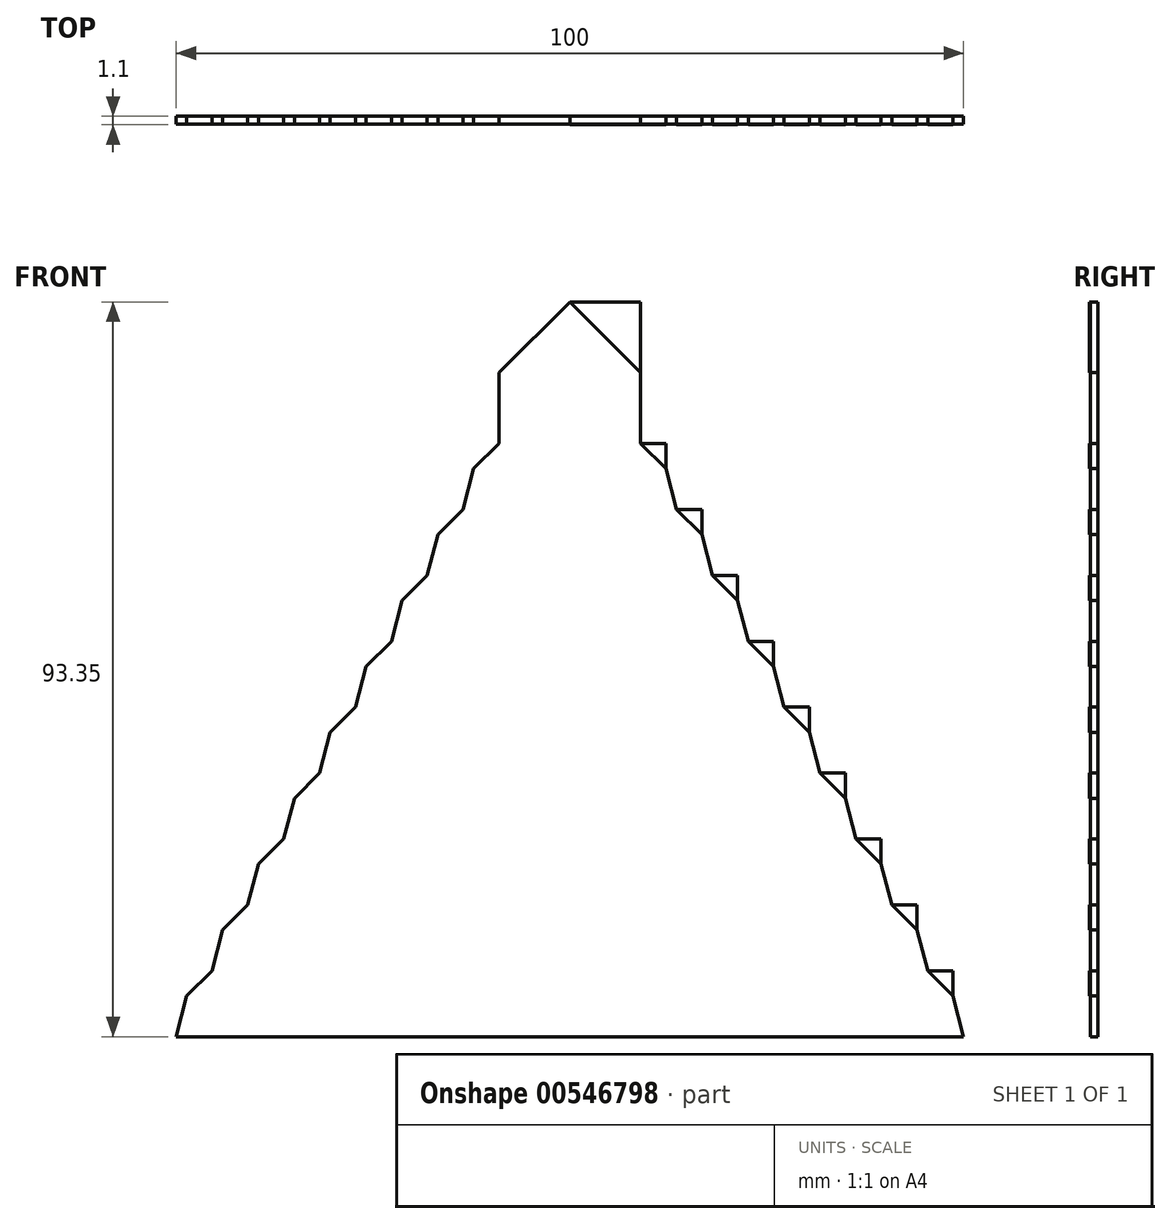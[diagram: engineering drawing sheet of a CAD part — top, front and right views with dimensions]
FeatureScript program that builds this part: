
annotation { "Feature Type Name" : "Feature", "Feature Type Description" : "" }
export const myFeature = defineFeature(function(context is Context, id is Id, definition is map)
    precondition{}
    {
        {
            var Q0;
            Q0=qCreatedBy(makeId("Front.planeOp"),FACE);
            var sketch = newSketch(context, id + "F0", { "sketchPlane" : qUnion([Q0])});
            skLineSegment(sketch, "E0.right", {"start": v(50, 0) * mm, "end": v(48.66, 5.18) * mm});
            skLineSegment(sketch, "E1", {"start": v(48.66, 5.18) * mm, "end": v(45.46, 8.38) * mm});
            skLineSegment(sketch, "E2.right", {"start": v(45.46, 8.38) * mm, "end": v(44.1, 13.55) * mm});
            skLineSegment(sketch, "E3", {"start": v(44.1, 13.55) * mm, "end": v(40.9, 16.75) * mm});
            skLineSegment(sketch, "E4.right", {"start": v(40.9, 16.75) * mm, "end": v(39.55, 21.92) * mm});
            skLineSegment(sketch, "E5", {"start": v(39.55, 21.92) * mm, "end": v(36.35, 25.12) * mm});
            skLineSegment(sketch, "E6.right", {"start": v(36.35, 25.12) * mm, "end": v(34.99, 30.3) * mm});
            skLineSegment(sketch, "E7", {"start": v(34.99, 30.3) * mm, "end": v(31.79, 33.5) * mm});
            skLineSegment(sketch, "E8.right", {"start": v(31.79, 33.5) * mm, "end": v(30.43, 38.66) * mm});
            skLineSegment(sketch, "E9", {"start": v(30.43, 38.66) * mm, "end": v(27.23, 41.86) * mm});
            skLineSegment(sketch, "E10.right", {"start": v(27.23, 41.86) * mm, "end": v(25.87, 47.04) * mm});
            skLineSegment(sketch, "E11", {"start": v(25.87, 47.04) * mm, "end": v(22.67, 50.24) * mm});
            skLineSegment(sketch, "E12.right", {"start": v(22.67, 50.24) * mm, "end": v(21.32, 55.4) * mm});
            skLineSegment(sketch, "E13", {"start": v(21.32, 55.4) * mm, "end": v(18.12, 58.6) * mm});
            skLineSegment(sketch, "E14.right", {"start": v(18.12, 58.6) * mm, "end": v(16.76, 63.78) * mm});
            skLineSegment(sketch, "E15", {"start": v(16.76, 63.78) * mm, "end": v(13.56, 66.98) * mm});
            skLineSegment(sketch, "E16.right", {"start": v(13.56, 66.98) * mm, "end": v(12.2, 72.15) * mm});
            skLineSegment(sketch, "E17", {"start": v(12.2, 72.15) * mm, "end": v(9, 75.35) * mm});
            skLineSegment(sketch, "E18", {"start": v(9, 75.35) * mm, "end": v(9, 84.35) * mm});
            skLineSegment(sketch, "E19", {"start": v(9, 84.35) * mm, "end": v(0, 93.35) * mm});
            skLineSegment(sketch, "E20", {"start": v(0, 93.35) * mm, "end": v(0, 0) * mm, "construction": true});
            skLineSegment(sketch, "E21.MirrorCS", {"start": v(-48.66, 5.18) * mm, "end": v(-45.46, 8.38) * mm});
            skLineSegment(sketch, "E22.MirrorCS", {"start": v(-45.46, 8.38) * mm, "end": v(-44.1, 13.55) * mm});
            skLineSegment(sketch, "E23.MirrorCS", {"start": v(-44.1, 13.55) * mm, "end": v(-40.9, 16.75) * mm});
            skLineSegment(sketch, "E24.MirrorCS", {"start": v(-40.9, 16.75) * mm, "end": v(-39.55, 21.92) * mm});
            skLineSegment(sketch, "E25.MirrorCS", {"start": v(-39.55, 21.92) * mm, "end": v(-36.35, 25.12) * mm});
            skLineSegment(sketch, "E26.MirrorCS", {"start": v(-36.35, 25.12) * mm, "end": v(-34.99, 30.3) * mm});
            skLineSegment(sketch, "E27.MirrorCS", {"start": v(-34.99, 30.3) * mm, "end": v(-31.79, 33.5) * mm});
            skLineSegment(sketch, "E28.MirrorCS", {"start": v(-31.79, 33.5) * mm, "end": v(-30.43, 38.66) * mm});
            skLineSegment(sketch, "E29.MirrorCS", {"start": v(-30.43, 38.66) * mm, "end": v(-27.23, 41.86) * mm});
            skLineSegment(sketch, "E30.MirrorCS", {"start": v(-27.23, 41.86) * mm, "end": v(-25.87, 47.04) * mm});
            skLineSegment(sketch, "E31.MirrorCS", {"start": v(-25.87, 47.04) * mm, "end": v(-22.67, 50.24) * mm});
            skLineSegment(sketch, "E32.MirrorCS", {"start": v(-13.56, 66.98) * mm, "end": v(-12.2, 72.15) * mm});
            skLineSegment(sketch, "E33.MirrorCS", {"start": v(-22.67, 50.24) * mm, "end": v(-21.32, 55.4) * mm});
            skLineSegment(sketch, "E34.MirrorCS", {"start": v(-12.2, 72.15) * mm, "end": v(-9, 75.35) * mm});
            skLineSegment(sketch, "E35.MirrorCS", {"start": v(-18.12, 58.6) * mm, "end": v(-16.76, 63.78) * mm});
            skLineSegment(sketch, "E36.MirrorCS", {"start": v(-16.76, 63.78) * mm, "end": v(-13.56, 66.98) * mm});
            skLineSegment(sketch, "E37.MirrorCS", {"start": v(-21.32, 55.4) * mm, "end": v(-18.12, 58.6) * mm});
            skLineSegment(sketch, "E38.MirrorCS", {"start": v(-50, 0) * mm, "end": v(-48.66, 5.18) * mm});
            skLineSegment(sketch, "E39.MirrorCS", {"start": v(-9, 75.35) * mm, "end": v(-9, 84.35) * mm});
            skLineSegment(sketch, "E40.MirrorCS", {"start": v(-9, 84.35) * mm, "end": v(0, 93.35) * mm});
            skLineSegment(sketch, "E41", {"start": v(50, 0) * mm, "end": v(-50, 0) * mm});
            skSolve(sketch);
        }
        {
            var Q0;
            Q0 = qSketchRegion(id + "F0", true);
            var Q1;
            Q1 = qConstructionFilter(qBodyType(qCreatedBy(id + "F0" ,EDGE), BodyType.WIRE), ConstructionObject.NO);
            extrude(context, id + "F1", {"entities" : qUnion([Q0]), "surfaceEntities" : qUnion([Q1]), "depth" : 1 * mm, "offsetDistance" : 25 * mm});
        }
        {
            var Q0;
            Q0=makeQuery(id+"F1.opExtrude","CAP_FACE",FACE,{"disambiguationData":[OSD([sQuery(id+"F0.wireOp",EDGE,"E0.right"),sQuery(id+"F0.wireOp",EDGE,"E1"),sQuery(id+"F0.wireOp",EDGE,"E2.right"),sQuery(id+"F0.wireOp",EDGE,"E3"),sQuery(id+"F0.wireOp",EDGE,"E4.right"),sQuery(id+"F0.wireOp",EDGE,"E5"),sQuery(id+"F0.wireOp",EDGE,"E6.right"),sQuery(id+"F0.wireOp",EDGE,"E7"),sQuery(id+"F0.wireOp",EDGE,"E8.right"),sQuery(id+"F0.wireOp",EDGE,"E9"),sQuery(id+"F0.wireOp",EDGE,"E10.right"),sQuery(id+"F0.wireOp",EDGE,"E11"),sQuery(id+"F0.wireOp",EDGE,"E12.right"),sQuery(id+"F0.wireOp",EDGE,"E13"),sQuery(id+"F0.wireOp",EDGE,"E14.right"),sQuery(id+"F0.wireOp",EDGE,"E15"),sQuery(id+"F0.wireOp",EDGE,"E16.right"),sQuery(id+"F0.wireOp",EDGE,"E17"),sQuery(id+"F0.wireOp",EDGE,"E18"),sQuery(id+"F0.wireOp",EDGE,"E19"),sQuery(id+"F0.wireOp",EDGE,"E21.MirrorCS"),sQuery(id+"F0.wireOp",EDGE,"E22.MirrorCS"),sQuery(id+"F0.wireOp",EDGE,"E23.MirrorCS"),sQuery(id+"F0.wireOp",EDGE,"E24.MirrorCS"),sQuery(id+"F0.wireOp",EDGE,"E25.MirrorCS"),sQuery(id+"F0.wireOp",EDGE,"E26.MirrorCS"),sQuery(id+"F0.wireOp",EDGE,"E27.MirrorCS"),sQuery(id+"F0.wireOp",EDGE,"E28.MirrorCS"),sQuery(id+"F0.wireOp",EDGE,"E29.MirrorCS"),sQuery(id+"F0.wireOp",EDGE,"E30.MirrorCS"),sQuery(id+"F0.wireOp",EDGE,"E31.MirrorCS"),sQuery(id+"F0.wireOp",EDGE,"E32.MirrorCS"),sQuery(id+"F0.wireOp",EDGE,"E33.MirrorCS"),sQuery(id+"F0.wireOp",EDGE,"E34.MirrorCS"),sQuery(id+"F0.wireOp",EDGE,"E35.MirrorCS"),sQuery(id+"F0.wireOp",EDGE,"E36.MirrorCS"),sQuery(id+"F0.wireOp",EDGE,"E37.MirrorCS"),sQuery(id+"F0.wireOp",EDGE,"E38.MirrorCS"),sQuery(id+"F0.wireOp",EDGE,"E39.MirrorCS"),sQuery(id+"F0.wireOp",EDGE,"E40.MirrorCS"),sQuery(id+"F0.wireOp",EDGE,"E41")])],"isStart":false});
            var sketch = newSketch(context, id + "F2", { "sketchPlane" : qUnion([Q0])});
            skLineSegment(sketch, "E42", {"start": v(-48.66, 5.18) * mm, "end": v(48.66, 5.18) * mm});
            skLineSegment(sketch, "E43", {"start": v(45.46, 8.38) * mm, "end": v(-45.46, 8.38) * mm});
            skLineSegment(sketch, "E44", {"start": v(-44.1, 13.55) * mm, "end": v(44.1, 13.55) * mm});
            skLineSegment(sketch, "E45", {"start": v(-40.9, 16.75) * mm, "end": v(40.9, 16.75) * mm});
            skLineSegment(sketch, "E46", {"start": v(39.55, 21.92) * mm, "end": v(-39.55, 21.92) * mm});
            skLineSegment(sketch, "E47", {"start": v(-36.35, 25.12) * mm, "end": v(36.35, 25.12) * mm});
            skLineSegment(sketch, "E48", {"start": v(-34.99, 30.3) * mm, "end": v(34.99, 30.3) * mm});
            skLineSegment(sketch, "E49", {"start": v(31.79, 33.5) * mm, "end": v(-31.79, 33.5) * mm});
            skLineSegment(sketch, "E50", {"start": v(30.43, 38.66) * mm, "end": v(-30.43, 38.66) * mm});
            skLineSegment(sketch, "E51", {"start": v(27.23, 41.86) * mm, "end": v(-27.23, 41.86) * mm});
            skLineSegment(sketch, "E52", {"start": v(-25.87, 47.04) * mm, "end": v(25.87, 47.04) * mm});
            skLineSegment(sketch, "E53", {"start": v(-22.67, 50.24) * mm, "end": v(22.67, 50.24) * mm});
            skLineSegment(sketch, "E54", {"start": v(-21.32, 55.4) * mm, "end": v(21.32, 55.4) * mm});
            skLineSegment(sketch, "E55", {"start": v(18.12, 58.6) * mm, "end": v(-18.12, 58.6) * mm});
            skLineSegment(sketch, "E56", {"start": v(-16.76, 63.78) * mm, "end": v(16.76, 63.78) * mm});
            skLineSegment(sketch, "E57", {"start": v(-13.56, 66.98) * mm, "end": v(13.56, 66.98) * mm});
            skLineSegment(sketch, "E58", {"start": v(-12.2, 72.15) * mm, "end": v(12.2, 72.15) * mm});
            skLineSegment(sketch, "E59", {"start": v(-9, 75.35) * mm, "end": v(9, 75.35) * mm});
            skLineSegment(sketch, "E60", {"start": v(-9, 84.35) * mm, "end": v(9, 84.35) * mm});
            skSolve(sketch);
        }
        {
            var Q0;
            Q0=makeQuery(id+"F2.imprint","IMPRINT",FACE,{"disambiguationData":[TD([[makeQuery(id+"F2.imprint","IMPRINT",EDGE,{"derivedFrom":sQuery(id+"F2.wireOp",EDGE,"E43")}),-1.0]])]});
            var sketch = newSketch(context, id + "F3", { "sketchPlane" : qUnion([Q0])});
            skLineSegment(sketch, "E61", {"start": v(48.66, 5.18) * mm, "end": v(48.66, 8.38) * mm});
            skLineSegment(sketch, "E62", {"start": v(48.66, 8.38) * mm, "end": v(45.46, 8.38) * mm});
            skLineSegment(sketch, "E63", {"start": v(44.1, 13.55) * mm, "end": v(44.1, 16.75) * mm});
            skLineSegment(sketch, "E64", {"start": v(44.1, 16.75) * mm, "end": v(40.9, 16.75) * mm});
            skLineSegment(sketch, "E65", {"start": v(39.55, 21.92) * mm, "end": v(39.55, 25.12) * mm});
            skLineSegment(sketch, "E66", {"start": v(39.55, 25.12) * mm, "end": v(36.35, 25.12) * mm});
            skLineSegment(sketch, "E67", {"start": v(34.99, 30.3) * mm, "end": v(34.99, 33.5) * mm});
            skLineSegment(sketch, "E68", {"start": v(34.99, 33.5) * mm, "end": v(31.79, 33.5) * mm});
            skLineSegment(sketch, "E69", {"start": v(30.43, 38.66) * mm, "end": v(30.43, 41.86) * mm});
            skLineSegment(sketch, "E70", {"start": v(30.43, 41.86) * mm, "end": v(27.23, 41.86) * mm});
            skLineSegment(sketch, "E71", {"start": v(25.87, 47.04) * mm, "end": v(25.87, 50.24) * mm});
            skLineSegment(sketch, "E72", {"start": v(25.87, 50.24) * mm, "end": v(22.67, 50.24) * mm});
            skLineSegment(sketch, "E73", {"start": v(21.32, 55.4) * mm, "end": v(21.32, 58.6) * mm});
            skLineSegment(sketch, "E74", {"start": v(21.32, 58.6) * mm, "end": v(18.12, 58.6) * mm});
            skLineSegment(sketch, "E75", {"start": v(16.76, 63.78) * mm, "end": v(16.76, 66.98) * mm});
            skLineSegment(sketch, "E76", {"start": v(16.76, 66.98) * mm, "end": v(13.56, 66.98) * mm});
            skLineSegment(sketch, "E77", {"start": v(12.2, 72.15) * mm, "end": v(12.2, 75.35) * mm});
            skLineSegment(sketch, "E78", {"start": v(12.2, 75.35) * mm, "end": v(9, 75.35) * mm});
            skLineSegment(sketch, "E79", {"start": v(9, 84.35) * mm, "end": v(9, 93.35) * mm});
            skLineSegment(sketch, "E80", {"start": v(9, 93.35) * mm, "end": v(0, 93.35) * mm});
            skLineSegment(sketch, "E81", {"start": v(0, 93.35) * mm, "end": v(9, 84.35) * mm});
            skLineSegment(sketch, "E82", {"start": v(9, 75.35) * mm, "end": v(12.2, 72.15) * mm});
            skLineSegment(sketch, "E83", {"start": v(13.56, 66.98) * mm, "end": v(16.76, 63.78) * mm});
            skLineSegment(sketch, "E84", {"start": v(18.12, 58.6) * mm, "end": v(21.32, 55.4) * mm});
            skLineSegment(sketch, "E85", {"start": v(22.67, 50.24) * mm, "end": v(25.87, 47.04) * mm});
            skLineSegment(sketch, "E86", {"start": v(27.23, 41.86) * mm, "end": v(30.43, 38.66) * mm});
            skLineSegment(sketch, "E87", {"start": v(31.79, 33.5) * mm, "end": v(34.99, 30.3) * mm});
            skLineSegment(sketch, "E88", {"start": v(36.35, 25.12) * mm, "end": v(39.55, 21.92) * mm});
            skLineSegment(sketch, "E89", {"start": v(40.9, 16.75) * mm, "end": v(44.1, 13.55) * mm});
            skLineSegment(sketch, "E90", {"start": v(45.46, 8.38) * mm, "end": v(48.66, 5.18) * mm});
            skSolve(sketch);
        }
        {
            var Q0;
            Q0 = qSketchRegion(id + "F3", true);
            extrude(context, id + "F4", {"entities" : qUnion([Q0]), "depth" : .1 * mm, "offsetDistance" : 25 * mm});
        }
    });
